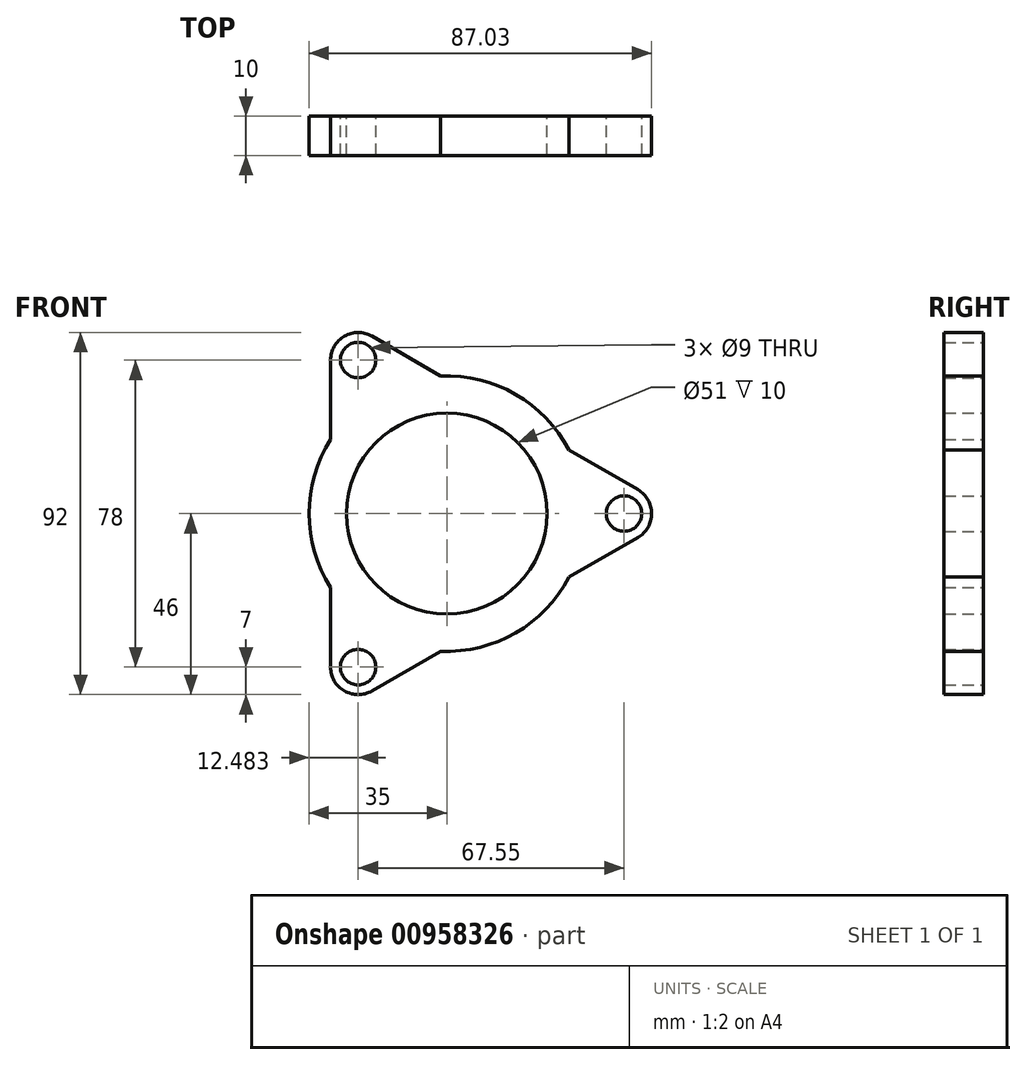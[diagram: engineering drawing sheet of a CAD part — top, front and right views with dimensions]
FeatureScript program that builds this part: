
annotation { "Feature Type Name" : "Feature", "Feature Type Description" : "" }
export const myFeature = defineFeature(function(context is Context, id is Id, definition is map)
    precondition{}
    {
        {
            var Q0;
            Q0=qCreatedBy(makeId("Front.planeOp"),FACE);
            var sketch = newSketch(context, id + "F0", { "sketchPlane" : qUnion([Q0])});
            skCircle(sketch, "E0", {"center": v(0, 0) * mm, "radius": 25.5 * mm});
            skCircle(sketch, "E1", {"center": v(45.03, 0) * mm, "radius": 4.5 * mm});
            skCircle(sketch, "E2", {"center": v(-22.52, 39) * mm, "radius": 4.5 * mm});
            skCircle(sketch, "E3", {"center": v(-22.52, -39) * mm, "radius": 4.5 * mm});
            skLineSegment(sketch, "E4", {"start": v(48.53, 6.06) * mm, "end": v(31.05, 16.16) * mm});
            skLineSegment(sketch, "E5", {"start": v(-19.02, 45.06) * mm, "end": v(-1.53, 34.97) * mm});
            skLineSegment(sketch, "E6", {"start": v(-29.52, 39) * mm, "end": v(-29.52, 18.8) * mm});
            skLineSegment(sketch, "E7", {"start": v(-29.52, -39) * mm, "end": v(-29.52, -18.8) * mm});
            skLineSegment(sketch, "E8", {"start": v(-19.02, -45.06) * mm, "end": v(-1.53, -34.97) * mm});
            skLineSegment(sketch, "E9", {"start": v(48.53, -6.06) * mm, "end": v(31.05, -16.16) * mm});
            skArc(sketch, "E10", {"start": v(-1.53, 34.97) * mm, "mid": v(17.5, 30.31) * mm, "end": v(31.05, 16.16) * mm});
            skArc(sketch, "E11", {"start": v(31.05, -16.16) * mm, "mid": v(17.5, -30.31) * mm, "end": v(-1.53, -34.97) * mm});
            skArc(sketch, "E12", {"start": v(-29.52, -18.8) * mm, "mid": v(-35, 0) * mm, "end": v(-29.52, 18.8) * mm});
            skArc(sketch, "E13", {"start": v(-29.52, 39) * mm, "mid": v(-26.02, 45.06) * mm, "end": v(-19.02, 45.06) * mm});
            skArc(sketch, "E14", {"start": v(48.53, 6.06) * mm, "mid": v(52.03, 0) * mm, "end": v(48.53, -6.06) * mm});
            skArc(sketch, "E15", {"start": v(-29.52, -39) * mm, "mid": v(-26.02, -45.06) * mm, "end": v(-19.02, -45.06) * mm});
            skSolve(sketch);
        }
        {
            var Q0;
            Q0 = qSketchRegion(id + "F0", true);
            extrude(context, id + "F1", {"entities" : qUnion([Q0]), "depth" : 10 * mm, "offsetDistance" : 25 * mm});
        }
    });
